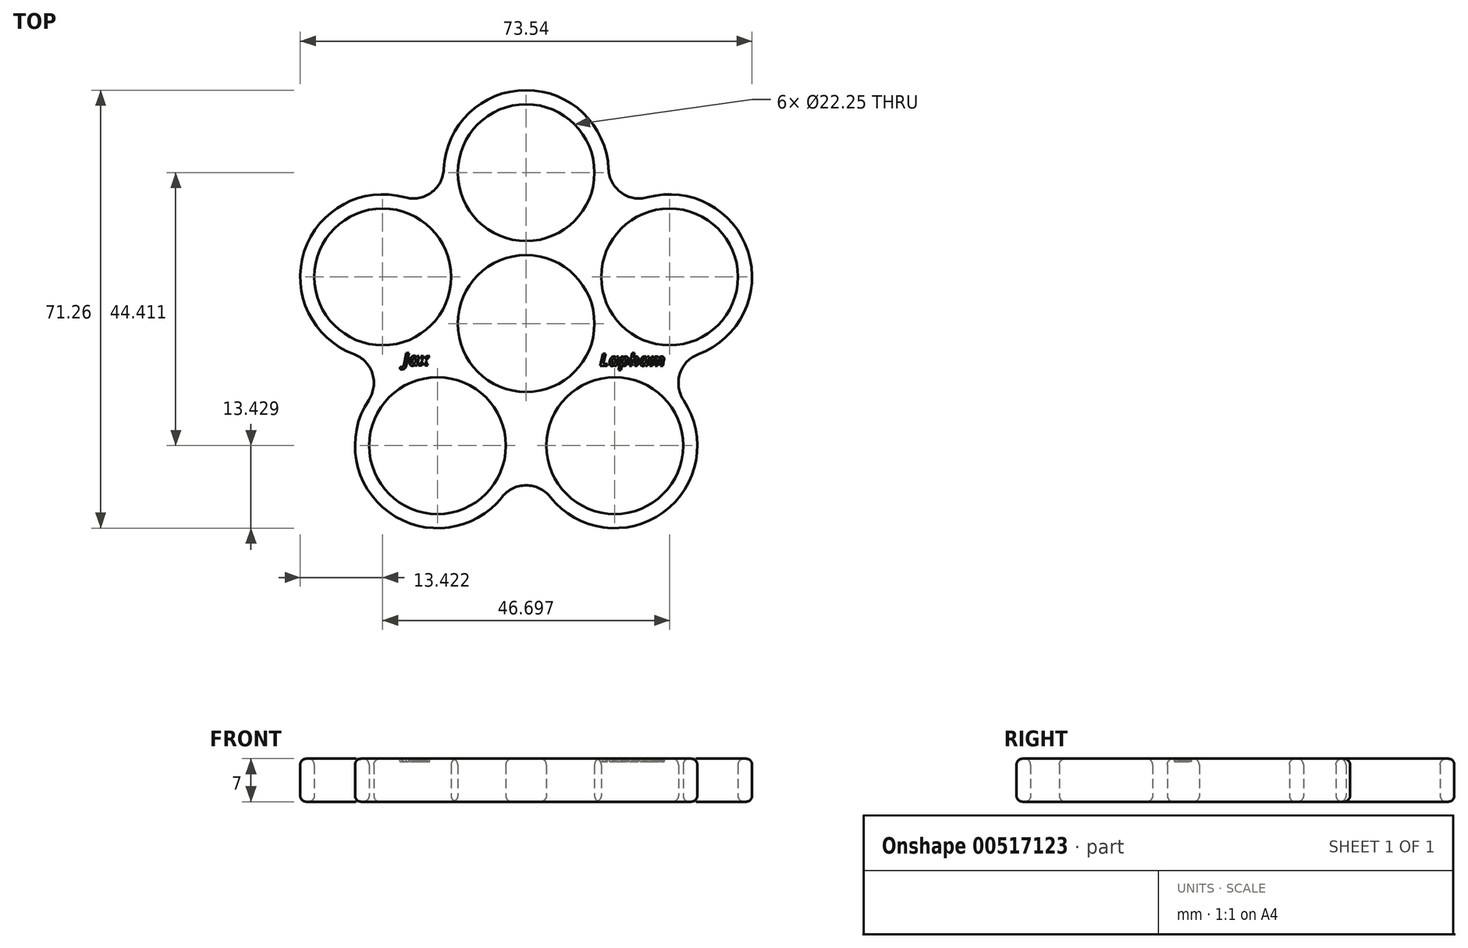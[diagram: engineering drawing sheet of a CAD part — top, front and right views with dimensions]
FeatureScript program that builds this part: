
annotation { "Feature Type Name" : "Feature", "Feature Type Description" : "" }
export const myFeature = defineFeature(function(context is Context, id is Id, definition is map)
    precondition{}
    {
        {
            var Q0;
            Q0=qCreatedBy(makeId("Top.planeOp"),FACE);
            var sketch = newSketch(context, id + "F0", { "sketchPlane" : qUnion([Q0])});
            skCircle(sketch, "E0", {"center": v(0, 0) * mm, "radius": 11.12 * mm});
            skLineSegment(sketch, "E1", {"start": v(0, 0) * mm, "end": v(0, 24.55) * mm, "construction": true});
            skLineSegment(sketch, "E2", {"start": v(0, 0) * mm, "end": v(23.35, 7.59) * mm, "construction": true});
            skLineSegment(sketch, "E3", {"start": v(0, 0) * mm, "end": v(14.43, -19.86) * mm, "construction": true});
            skLineSegment(sketch, "E4", {"start": v(0, 0) * mm, "end": v(-23.35, 7.59) * mm, "construction": true});
            skLineSegment(sketch, "E5", {"start": v(0, 0) * mm, "end": v(-14.43, -19.86) * mm, "construction": true});
            skCircle(sketch, "E6", {"center": v(0, 24.55) * mm, "radius": 11.12 * mm});
            skCircle(sketch, "E7", {"center": v(-23.35, 7.59) * mm, "radius": 11.12 * mm});
            skCircle(sketch, "E8", {"center": v(-14.43, -19.86) * mm, "radius": 11.12 * mm});
            skCircle(sketch, "E9", {"center": v(14.43, -19.86) * mm, "radius": 11.12 * mm});
            skCircle(sketch, "E10", {"center": v(23.35, 7.59) * mm, "radius": 11.12 * mm});
            skArc(sketch, "E11", {"start": v(13.41, 25.12) * mm, "mid": v(0, 37.97) * mm, "end": v(-13.41, 25.12) * mm});
            skArc(sketch, "E12", {"start": v(-19.75, 20.52) * mm, "mid": v(-36.12, 11.73) * mm, "end": v(-28.04, -5) * mm});
            skArc(sketch, "E13", {"start": v(-25.62, -12.44) * mm, "mid": v(-22.32, -30.72) * mm, "end": v(-3.92, -28.2) * mm});
            skArc(sketch, "E14", {"start": v(3.92, -28.2) * mm, "mid": v(22.32, -30.72) * mm, "end": v(25.62, -12.44) * mm});
            skArc(sketch, "E15", {"start": v(28.04, -5) * mm, "mid": v(36.12, 11.73) * mm, "end": v(19.75, 20.52) * mm});
            skArc(sketch, "E16", {"start": v(-19.75, 20.52) * mm, "mid": v(-15.47, 21.3) * mm, "end": v(-13.41, 25.12) * mm});
            skArc(sketch, "E17", {"start": v(-25.62, -12.44) * mm, "mid": v(-25.03, -8.13) * mm, "end": v(-28.04, -5) * mm});
            skArc(sketch, "E18", {"start": v(3.92, -28.2) * mm, "mid": v(0, -26.32) * mm, "end": v(-3.92, -28.2) * mm});
            skArc(sketch, "E19", {"start": v(13.41, 25.12) * mm, "mid": v(15.47, 21.3) * mm, "end": v(19.75, 20.52) * mm});
            skArc(sketch, "E20", {"start": v(28.04, -5) * mm, "mid": v(25.03, -8.13) * mm, "end": v(25.62, -12.44) * mm});
            skSolve(sketch);
        }
        {
            var Q0;
            Q0=makeQuery(id+"F0.imprint","IMPRINT",FACE,{"disambiguationData":[TD([[makeQuery(id+"F0.imprint","IMPRINT",EDGE,{"derivedFrom":sQuery(id+"F0.wireOp",EDGE,"E0")}),-1.0]])]});
            extrude(context, id + "F1", {"entities" : qUnion([Q0]), "depth" : 7 * mm});
        }
        {
            var Q0;
            Q0=makeQuery(id+"F1.opExtrude","CAP_EDGE",EDGE,{"disambiguationData":[OSD([sQuery(id+"F0.wireOp",EDGE,"E12")])],"isStart":false});
            var Q1;
            Q1=makeQuery(id+"F1.opExtrude","CAP_EDGE",EDGE,{"disambiguationData":[OSD([sQuery(id+"F0.wireOp",EDGE,"E13")])],"isStart":true});
            var Q2;
            Q2=makeQuery(id+"F1.opExtrude","CAP_EDGE",EDGE,{"disambiguationData":[OSD([sQuery(id+"F0.wireOp",EDGE,"E8")])],"isStart":false});
            var Q3;
            Q3=makeQuery(id+"F1.opExtrude","CAP_EDGE",EDGE,{"disambiguationData":[OSD([sQuery(id+"F0.wireOp",EDGE,"E7")])],"isStart":false});
            var Q4;
            Q4=makeQuery(id+"F1.opExtrude","CAP_EDGE",EDGE,{"disambiguationData":[OSD([sQuery(id+"F0.wireOp",EDGE,"E6")])],"isStart":true});
            var Q5;
            Q5=makeQuery(id+"F1.opExtrude","CAP_EDGE",EDGE,{"disambiguationData":[OSD([sQuery(id+"F0.wireOp",EDGE,"E6")])],"isStart":false});
            var Q6;
            Q6=makeQuery(id+"F1.opExtrude","CAP_EDGE",EDGE,{"disambiguationData":[OSD([sQuery(id+"F0.wireOp",EDGE,"E7")])],"isStart":true});
            var Q7;
            Q7=makeQuery(id+"F1.opExtrude","CAP_EDGE",EDGE,{"disambiguationData":[OSD([sQuery(id+"F0.wireOp",EDGE,"E8")])],"isStart":true});
            var Q8;
            Q8=makeQuery(id+"F1.opExtrude","CAP_EDGE",EDGE,{"disambiguationData":[OSD([sQuery(id+"F0.wireOp",EDGE,"E0")])],"isStart":true});
            var Q9;
            Q9=makeQuery(id+"F1.opExtrude","CAP_EDGE",EDGE,{"disambiguationData":[OSD([sQuery(id+"F0.wireOp",EDGE,"E0")])],"isStart":false});
            var Q10;
            Q10=makeQuery(id+"F1.opExtrude","CAP_EDGE",EDGE,{"disambiguationData":[OSD([sQuery(id+"F0.wireOp",EDGE,"E10")])],"isStart":true});
            var Q11;
            Q11=makeQuery(id+"F1.opExtrude","CAP_EDGE",EDGE,{"disambiguationData":[OSD([sQuery(id+"F0.wireOp",EDGE,"E10")])],"isStart":false});
            var Q12;
            Q12=makeQuery(id+"F1.opExtrude","CAP_EDGE",EDGE,{"disambiguationData":[OSD([sQuery(id+"F0.wireOp",EDGE,"E9")])],"isStart":true});
            var Q13;
            Q13=makeQuery(id+"F1.opExtrude","CAP_EDGE",EDGE,{"disambiguationData":[OSD([sQuery(id+"F0.wireOp",EDGE,"E9")])],"isStart":false});
            fillet(context, id + "F2", {"entities" : qUnion([Q0, Q1, Q2, Q3, Q4, Q5, Q6, Q7, Q8, Q9, Q10, Q11, Q12, Q13]), "radius" : 1 * mm, "tangentPropagation" : true, "allowEdgeOverflow" : false});
        }
        {
            var Q0;
            Q0=makeQuery(id+"F2.opFillet","SPLIT",FACE,{"disambiguationData":[OD(1.0)],"derivedFrom":makeQuery(id+"F1.opExtrude","CAP_FACE",FACE,{"disambiguationData":[OSD([sQuery(id+"F0.wireOp",EDGE,"E0"),sQuery(id+"F0.wireOp",EDGE,"E6"),sQuery(id+"F0.wireOp",EDGE,"E7"),sQuery(id+"F0.wireOp",EDGE,"E8"),sQuery(id+"F0.wireOp",EDGE,"E9"),sQuery(id+"F0.wireOp",EDGE,"E10"),sQuery(id+"F0.wireOp",EDGE,"E11"),sQuery(id+"F0.wireOp",EDGE,"E12"),sQuery(id+"F0.wireOp",EDGE,"E13"),sQuery(id+"F0.wireOp",EDGE,"E14"),sQuery(id+"F0.wireOp",EDGE,"E15"),sQuery(id+"F0.wireOp",EDGE,"E16"),sQuery(id+"F0.wireOp",EDGE,"E17"),sQuery(id+"F0.wireOp",EDGE,"E18"),sQuery(id+"F0.wireOp",EDGE,"E19"),sQuery(id+"F0.wireOp",EDGE,"E20")])],"isStart":false})});
            var sketch = newSketch(context, id + "F3", { "sketchPlane" : qUnion([Q0])});
            skText(sketch, "E21", { "text": "Jax", "fontName": "OpenSans-BoldItalic.ttf"});
            const initialGuessF3  = {"E21": [-0.02005, -0.00685, 1, 0, 0.00208]};
            skSetInitialGuess(sketch, initialGuessF3);
            skSolve(sketch);
        }
        {
            var Q0;
            Q0 = qSketchRegion(id + "F3", true);
            extrude(context, id + "F4", {"entities" : qUnion([Q0]), "operationType" : NewBodyOperationType.REMOVE, "oppositeDirection" : true, "depth" : .5 * mm, "offsetDistance" : 25 * mm});
        }
        {
            var Q0;
            Q0=makeQuery(id+"F2.opFillet","SPLIT",FACE,{"disambiguationData":[OD(4.0)],"derivedFrom":makeQuery(id+"F1.opExtrude","CAP_FACE",FACE,{"disambiguationData":[OSD([sQuery(id+"F0.wireOp",EDGE,"E0"),sQuery(id+"F0.wireOp",EDGE,"E6"),sQuery(id+"F0.wireOp",EDGE,"E7"),sQuery(id+"F0.wireOp",EDGE,"E8"),sQuery(id+"F0.wireOp",EDGE,"E9"),sQuery(id+"F0.wireOp",EDGE,"E10"),sQuery(id+"F0.wireOp",EDGE,"E11"),sQuery(id+"F0.wireOp",EDGE,"E12"),sQuery(id+"F0.wireOp",EDGE,"E13"),sQuery(id+"F0.wireOp",EDGE,"E14"),sQuery(id+"F0.wireOp",EDGE,"E15"),sQuery(id+"F0.wireOp",EDGE,"E16"),sQuery(id+"F0.wireOp",EDGE,"E17"),sQuery(id+"F0.wireOp",EDGE,"E18"),sQuery(id+"F0.wireOp",EDGE,"E19"),sQuery(id+"F0.wireOp",EDGE,"E20")])],"isStart":false})});
            var sketch = newSketch(context, id + "F5", { "sketchPlane" : qUnion([Q0])});
            skPoint(sketch, "E22.firstSnap0", {"position": v(11.41, -3.7) * mm});
            skText(sketch, "E23", { "text": "Lapham", "fontName": "OpenSans-BoldItalic.ttf"});
            const initialGuessF5  = {"E23": [0.01201, -0.00689, 1, 0, 0.002]};
            skSetInitialGuess(sketch, initialGuessF5);
            skSolve(sketch);
        }
        {
            var Q0;
            Q0 = qSketchRegion(id + "F5", true);
            extrude(context, id + "F6", {"entities" : qUnion([Q0]), "operationType" : NewBodyOperationType.REMOVE, "oppositeDirection" : true, "depth" : .5 * mm, "offsetDistance" : 25 * mm});
        }
    });
